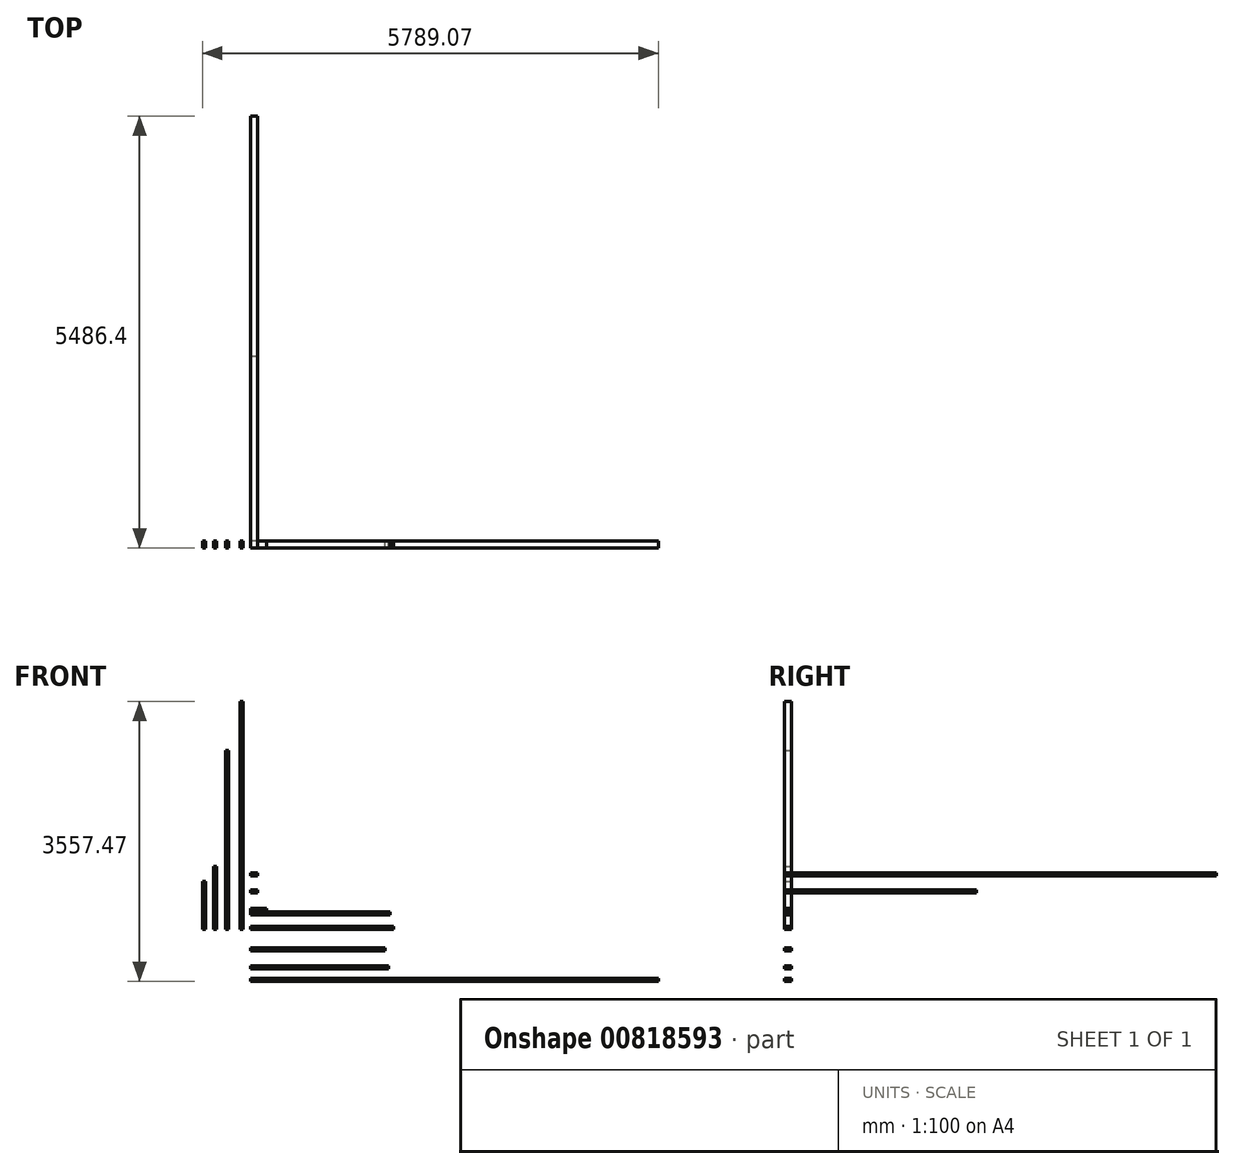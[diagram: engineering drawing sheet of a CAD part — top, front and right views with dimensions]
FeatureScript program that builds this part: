
annotation { "Feature Type Name" : "Feature", "Feature Type Description" : "" }
export const myFeature = defineFeature(function(context is Context, id is Id, definition is map)
    precondition{}
    {
        {
            var Q0;
            Q0=qCreatedBy(makeId("Right.planeOp"),FACE);
            var sketch = newSketch(context, id + "F0", { "sketchPlane" : qUnion([Q0])});
            skLineSegment(sketch, "E0.bottom", {"start": v(0, 0) * mm, "end": v(88.9, 0) * mm});
            skLineSegment(sketch, "E0.top", {"start": v(0, 38.1) * mm, "end": v(88.9, 38.1) * mm});
            skLineSegment(sketch, "E0.left", {"start": v(0, 0) * mm, "end": v(0, 38.1) * mm});
            skLineSegment(sketch, "E0.right", {"start": v(88.9, 0) * mm, "end": v(88.9, 38.1) * mm});
            skSolve(sketch);
        }
        {
            var Q0;
            Q0 = qSketchRegion(id + "F0", true);
            extrude(context, id + "F1", {"entities" : qUnion([Q0]), "depth" : 1816.1 * mm, "offsetDistance" : 25.4 * mm});
        }
        {
            var Q0;
            Q0=qCreatedBy(makeId("Right.planeOp"),FACE);
            var sketch = newSketch(context, id + "F2", { "sketchPlane" : qUnion([Q0])});
            skLineSegment(sketch, "E1.bottom", {"start": v(0, 229.22) * mm, "end": v(88.9, 229.22) * mm});
            skLineSegment(sketch, "E1.top", {"start": v(0, 267.32) * mm, "end": v(88.9, 267.32) * mm});
            skLineSegment(sketch, "E1.left", {"start": v(0, 229.22) * mm, "end": v(0, 267.32) * mm});
            skLineSegment(sketch, "E1.right", {"start": v(88.9, 229.22) * mm, "end": v(88.9, 267.32) * mm});
            skSolve(sketch);
        }
        {
            var Q0;
            Q0 = qSketchRegion(id + "F2", true);
            extrude(context, id + "F3", {"entities" : qUnion([Q0]), "depth" : ((18 * 12) - 7) * mm, "offsetDistance" : 25.4 * mm});
        }
        {
            var Q0;
            Q0=qCreatedBy(makeId("Top.planeOp"),FACE);
            var sketch = newSketch(context, id + "F4", { "sketchPlane" : qUnion([Q0])});
            skLineSegment(sketch, "E2.bottom", {"start": v(-93.15, 0) * mm, "end": v(-131.25, 0) * mm});
            skLineSegment(sketch, "E2.top", {"start": v(-93.15, 88.9) * mm, "end": v(-131.25, 88.9) * mm});
            skLineSegment(sketch, "E2.left", {"start": v(-93.15, 0) * mm, "end": v(-93.15, 88.9) * mm});
            skLineSegment(sketch, "E2.right", {"start": v(-131.25, 0) * mm, "end": v(-131.25, 88.9) * mm});
            skSolve(sketch);
        }
        {
            var Q0;
            Q0 = qSketchRegion(id + "F4", true);
            extrude(context, id + "F5", {"entities" : qUnion([Q0]), "depth" : 2895.6 * mm, "offsetDistance" : 25.4 * mm});
        }
        {
            var Q0;
            Q0=qCreatedBy(makeId("Right.planeOp"),FACE);
            var sketch = newSketch(context, id + "F6", { "sketchPlane" : qUnion([Q0])});
            skLineSegment(sketch, "E3.bottom", {"start": v(0, 184.85) * mm, "end": v(88.9, 184.85) * mm});
            skLineSegment(sketch, "E3.top", {"start": v(0, 222.95) * mm, "end": v(88.9, 222.95) * mm});
            skLineSegment(sketch, "E3.left", {"start": v(0, 184.85) * mm, "end": v(0, 222.95) * mm});
            skLineSegment(sketch, "E3.right", {"start": v(88.9, 184.85) * mm, "end": v(88.9, 222.95) * mm});
            skSolve(sketch);
        }
        {
            var Q0;
            Q0 = qSketchRegion(id + "F6", true);
            extrude(context, id + "F7", {"entities" : qUnion([Q0]), "depth" : 1778 * mm, "offsetDistance" : 25.4 * mm});
        }
        {
            var Q0;
            Q0=qCreatedBy(makeId("Top.planeOp"),FACE);
            var sketch = newSketch(context, id + "F8", { "sketchPlane" : qUnion([Q0])});
            skLineSegment(sketch, "E4.bottom", {"start": v(-276.06, 0) * mm, "end": v(-314.16, 0) * mm});
            skLineSegment(sketch, "E4.top", {"start": v(-276.06, 88.9) * mm, "end": v(-314.16, 88.9) * mm});
            skLineSegment(sketch, "E4.left", {"start": v(-276.06, 0) * mm, "end": v(-276.06, 88.9) * mm});
            skLineSegment(sketch, "E4.right", {"start": v(-314.16, 0) * mm, "end": v(-314.16, 88.9) * mm});
            skSolve(sketch);
        }
        {
            var Q0;
            Q0 = qSketchRegion(id + "F8", true);
            extrude(context, id + "F9", {"entities" : qUnion([Q0]), "depth" : 2273.3 * mm, "offsetDistance" : 25.4 * mm});
        }
        {
            var Q0;
            Q0=qCreatedBy(makeId("Front.planeOp"),FACE);
            var sketch = newSketch(context, id + "F10", { "sketchPlane" : qUnion([Q0])});
            skLineSegment(sketch, "E5.bottom", {"start": v(0, 460.34) * mm, "end": v(88.9, 460.34) * mm});
            skLineSegment(sketch, "E5.top", {"start": v(0, 498.44) * mm, "end": v(88.9, 498.44) * mm});
            skLineSegment(sketch, "E5.left", {"start": v(0, 460.34) * mm, "end": v(0, 498.44) * mm});
            skLineSegment(sketch, "E5.right", {"start": v(88.9, 460.34) * mm, "end": v(88.9, 498.44) * mm});
            skSolve(sketch);
        }
        {
            var Q0;
            Q0 = qSketchRegion(id + "F10", true);
            extrude(context, id + "F11", {"entities" : qUnion([Q0]), "oppositeDirection" : true, "depth" : 2438.4 * mm, "offsetDistance" : 25.4 * mm});
        }
        {
            var Q0;
            Q0=qCreatedBy(makeId("Top.planeOp"),FACE);
            var sketch = newSketch(context, id + "F12", { "sketchPlane" : qUnion([Q0])});
            skLineSegment(sketch, "E6.bottom", {"start": v(-569.37, 0) * mm, "end": v(-607.47, 0) * mm});
            skLineSegment(sketch, "E6.top", {"start": v(-569.37, 88.9) * mm, "end": v(-607.47, 88.9) * mm});
            skLineSegment(sketch, "E6.left", {"start": v(-569.37, 0) * mm, "end": v(-569.37, 88.9) * mm});
            skLineSegment(sketch, "E6.right", {"start": v(-607.47, 0) * mm, "end": v(-607.47, 88.9) * mm});
            skSolve(sketch);
        }
        {
            var Q0;
            Q0 = qSketchRegion(id + "F12", true);
            extrude(context, id + "F13", {"entities" : qUnion([Q0]), "depth" : 609.6 * mm, "offsetDistance" : 25.4 * mm});
        }
        {
            var Q0;
            Q0=qCreatedBy(makeId("Top.planeOp"),FACE);
            var sketch = newSketch(context, id + "F14", { "sketchPlane" : qUnion([Q0])});
            skLineSegment(sketch, "E7.bottom", {"start": v(-430.54, 0) * mm, "end": v(-468.64, 0) * mm});
            skLineSegment(sketch, "E7.top", {"start": v(-430.54, 88.9) * mm, "end": v(-468.64, 88.9) * mm});
            skLineSegment(sketch, "E7.left", {"start": v(-430.54, 0) * mm, "end": v(-430.54, 88.9) * mm});
            skLineSegment(sketch, "E7.right", {"start": v(-468.64, 0) * mm, "end": v(-468.64, 88.9) * mm});
            skSolve(sketch);
        }
        {
            var Q0;
            Q0 = qSketchRegion(id + "F14", true);
            extrude(context, id + "F15", {"entities" : qUnion([Q0]), "depth" : 800.1 * mm, "offsetDistance" : 25.4 * mm});
        }
        {
            var Q0;
            Q0=qCreatedBy(makeId("Front.planeOp"),FACE);
            var sketch = newSketch(context, id + "F16", { "sketchPlane" : qUnion([Q0])});
            skLineSegment(sketch, "E8.bottom", {"start": v(0, 678.63) * mm, "end": v(88.9, 678.63) * mm});
            skLineSegment(sketch, "E8.top", {"start": v(0, 716.73) * mm, "end": v(88.9, 716.73) * mm});
            skLineSegment(sketch, "E8.left", {"start": v(0, 678.63) * mm, "end": v(0, 716.73) * mm});
            skLineSegment(sketch, "E8.right", {"start": v(88.9, 678.63) * mm, "end": v(88.9, 716.73) * mm});
            skSolve(sketch);
        }
        {
            var Q0;
            Q0 = qSketchRegion(id + "F16", true);
            extrude(context, id + "F17", {"entities" : qUnion([Q0]), "oppositeDirection" : true, "depth" : 5486.4 * mm, "offsetDistance" : 25.4 * mm});
        }
        {
            var Q0;
            Q0=qCreatedBy(makeId("Right.planeOp"),FACE);
            var sketch = newSketch(context, id + "F18", { "sketchPlane" : qUnion([Q0])});
            skLineSegment(sketch, "E9.bottom", {"start": v(0, -237.44) * mm, "end": v(88.9, -237.44) * mm});
            skLineSegment(sketch, "E9.top", {"start": v(0, -275.54) * mm, "end": v(88.9, -275.54) * mm});
            skLineSegment(sketch, "E9.left", {"start": v(0, -237.44) * mm, "end": v(0, -275.54) * mm});
            skLineSegment(sketch, "E9.right", {"start": v(88.9, -237.44) * mm, "end": v(88.9, -275.54) * mm});
            skSolve(sketch);
        }
        {
            var Q0;
            Q0 = qSketchRegion(id + "F18", true);
            extrude(context, id + "F19", {"entities" : qUnion([Q0]), "depth" : 1714.5 * mm, "offsetDistance" : 25.4 * mm});
        }
        {
            var Q0;
            Q0=qCreatedBy(makeId("Right.planeOp"),FACE);
            var sketch = newSketch(context, id + "F20", { "sketchPlane" : qUnion([Q0])});
            skLineSegment(sketch, "E10.bottom", {"start": v(0, -623.77) * mm, "end": v(88.9, -623.77) * mm});
            skLineSegment(sketch, "E10.top", {"start": v(0, -661.87) * mm, "end": v(88.9, -661.87) * mm});
            skLineSegment(sketch, "E10.left", {"start": v(0, -623.77) * mm, "end": v(0, -661.87) * mm});
            skLineSegment(sketch, "E10.right", {"start": v(88.9, -623.77) * mm, "end": v(88.9, -661.87) * mm});
            skSolve(sketch);
        }
        {
            var Q0;
            Q0 = qSketchRegion(id + "F20", true);
            extrude(context, id + "F21", {"entities" : qUnion([Q0]), "depth" : 5181.6 * mm, "offsetDistance" : 25.4 * mm});
        }
        {
            var Q0;
            Q0=qCreatedBy(makeId("Right.planeOp"),FACE);
            var sketch = newSketch(context, id + "F22", { "sketchPlane" : qUnion([Q0])});
            skLineSegment(sketch, "E11.bottom", {"start": v(0, -504.94) * mm, "end": v(88.9, -504.94) * mm});
            skLineSegment(sketch, "E11.top", {"start": v(0, -466.84) * mm, "end": v(88.9, -466.84) * mm});
            skLineSegment(sketch, "E11.left", {"start": v(0, -504.94) * mm, "end": v(0, -466.84) * mm});
            skLineSegment(sketch, "E11.right", {"start": v(88.9, -504.94) * mm, "end": v(88.9, -466.84) * mm});
            skSolve(sketch);
        }
        {
            var Q0;
            Q0 = qSketchRegion(id + "F22", true);
            extrude(context, id + "F23", {"entities" : qUnion([Q0]), "depth" : 1752.6 * mm, "offsetDistance" : 25.4 * mm});
        }
    });
